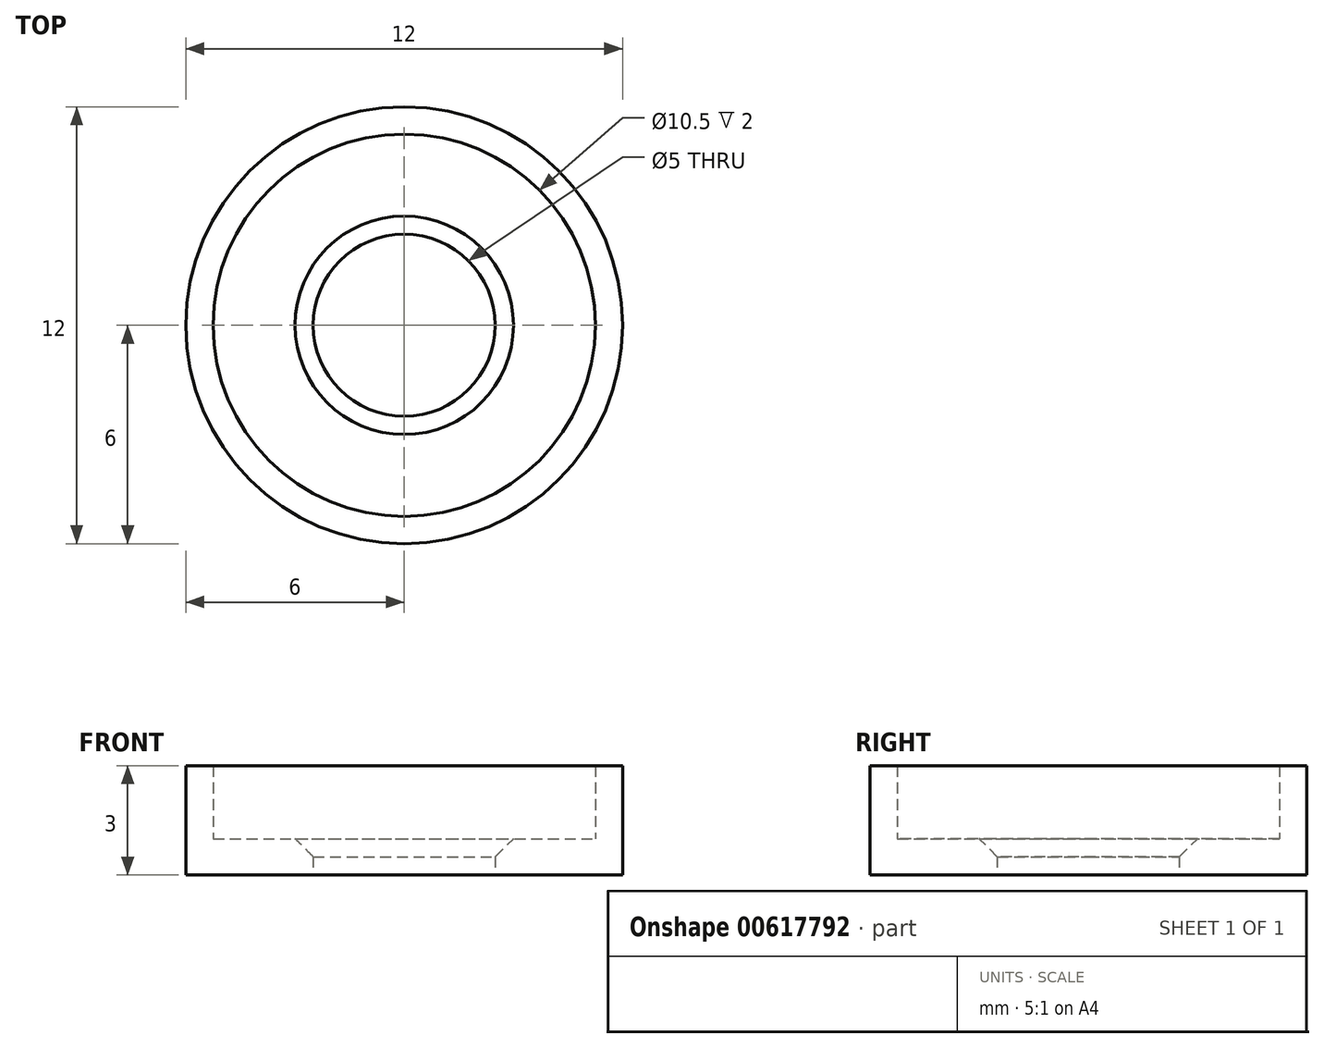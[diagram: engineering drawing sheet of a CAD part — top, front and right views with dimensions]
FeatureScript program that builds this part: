
annotation { "Feature Type Name" : "Feature", "Feature Type Description" : "" }
export const myFeature = defineFeature(function(context is Context, id is Id, definition is map)
    precondition{}
    {
        {
            var Q0;
            Q0=qCreatedBy(makeId("Front.planeOp"),FACE);
            var sketch = newSketch(context, id + "F0", { "sketchPlane" : qUnion([Q0])});
            skLineSegment(sketch, "E0", {"start": v(0, 0) * mm, "end": v(0, 3) * mm, "construction": true});
            skLineSegment(sketch, "E1", {"start": v(6, 0) * mm, "end": v(6, 3) * mm});
            skLineSegment(sketch, "E2", {"start": v(6, 3) * mm, "end": v(5.25, 3) * mm});
            skLineSegment(sketch, "E3", {"start": v(2.5, 0) * mm, "end": v(6, 0) * mm});
            skLineSegment(sketch, "E4", {"start": v(2.5, 0) * mm, "end": v(2.5, 1) * mm});
            skLineSegment(sketch, "E5", {"start": v(2.5, 1) * mm, "end": v(5.25, 1) * mm});
            skLineSegment(sketch, "E6", {"start": v(5.25, 1) * mm, "end": v(5.25, 3) * mm});
            skSolve(sketch);
        }
        {
            var Q0;
            Q0=makeQuery(id+"F0.imprint","IMPRINT",FACE,{"disambiguationData":[TD([[makeQuery(id+"F0.imprint","IMPRINT",EDGE,{"derivedFrom":sQuery(id+"F0.wireOp",EDGE,"E1")}),1.0]])]});
            var Q1;
            Q1=sQuery(id+"F0.wireOp",EDGE,"E0");
            revolve(context, id + "F1", {"entities" : qUnion([Q0]), "axis" : qUnion([Q1]), "revolveType" : RevolveType.FULL});
        }
        {
            var Q0;
            Q0=makeQuery(id+"F1.opRevolve","SWEPT_EDGE",EDGE,{"disambiguationData":[OSD([sQuery(id+"F0.wireOp",EDGE,"E4"),sQuery(id+"F0.wireOp",EDGE,"E5")])]});
            chamfer(context, id + "F2", {"entities" : qUnion([Q0]), "width" : 0.5 * mm, "tangentPropagation" : true});
        }
    });
